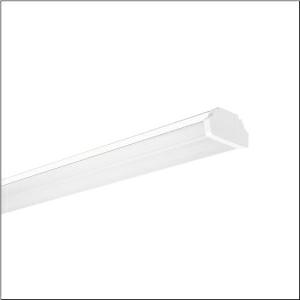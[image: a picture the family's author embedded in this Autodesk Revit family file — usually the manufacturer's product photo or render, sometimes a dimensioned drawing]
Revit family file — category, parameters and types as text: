
# Revit family: dus_r__31_mo_53bd812m1v4085_035f
name_source: partatom
category: Lighting Fixtures
units: mm (PartAtom-declared; Revit-internal decimal feet)

## family parameters
Cut with Voids When Loaded = No
Host = Face
Light Source = No
Part Type = Normal
Room Calculation Point = No
Round Connector Dimension = Use Diameter
Shared = No

## types (1)
- --- (1 x LED, 8950 lm, 59.6 W, 4000K)
    Apparent Load = 60 VA
    CIE Flux Codes = 47 80 95 92 100
    Color Rendering = 80
    Color Temperature = 4000K
    Default Elevation = 1800 mm
    Description = DUS® 31 MO, luminaire insert, of sheet steel, coil coated, white, length: 1.535mm, width: 81mm, height: 90mm, 5x system unit, system units: 307mm, LED rated luminous flux: 8.950lm, light colour: 840, control gear: ON/OFF Multilumen, control gear: ECG Multilumen, with plug, 3-pole, with phase selection, mains connection: 220..240V, AC, 50/60Hz, rated input power: 60W, through-wiring accessed according to module size, primary optical cover: cover, of PMMA, light emission: direct distribution, primary light characteristic: symmetric, protection rating (complete): IP20, protection rating (LED compartment): IP50, insulation class (complete): insulation class I (protective earthing), certification: CE, ENEC, VDE, UKCA, impact resistance: IK03, permissible ambient temperature for indoor applications: -35..+30°C, corresponds to IFS (International Featured Standards) requirements for safety and quality in the food industry, reducing of maximum allowable ambient temperature of 5°C with ceiling mounting, packaging unit: 1 piece
    Height = 95 mm
    Lamp = 1 x LED
    Lamp Light Flux = 8950 lm
    Lamp Power = 59.6 W
    Lamp count = 1
    Length = 1535 mm
    Luminous efficacy = 150 lm/W
    Manufacturer = Siteco
    ModVariant = No
    Model = 53BD812M1V4085
    Mounting Place = Ceiling
    Mounting Type = Pendant
    Number of Poles = 1
    OnlyDefault = Yes
    Power Factor = 1
    Product Name = DUS® 31 MO
    Product group = luminaire insert
    ProductGroupID = 901
    Protection Class = Protection class I
    Protection Degree = IP 20
    RLX_Detail_Level = 1
    RLX_Emergency_Light_Flux = 0 lm
    RLX_Emergency_Type = 0
    RLX_Emergency_Type_DB = No
    RlxData = <blob elided: 39829 chars, md5=7657a86e>
    Socket = socket
    Standby Power = 0 W
    System Light Flux = 8950 lm
    System Power = 60 W
    Type Comments = factory setting: luminous flux: 100 % | (A | C | E) | 129 mA
    Type Image = l_1313537.jpg
    URL = http://relux.com
    VarID = @adj_156273
    Voltage = 0 V
    Weight = 0.00 kg
    Width = 81 mm

## geometry (parser evidence)
native form markers: Blend x4, Sweep x11
no freeform markers — native parametric forms only
